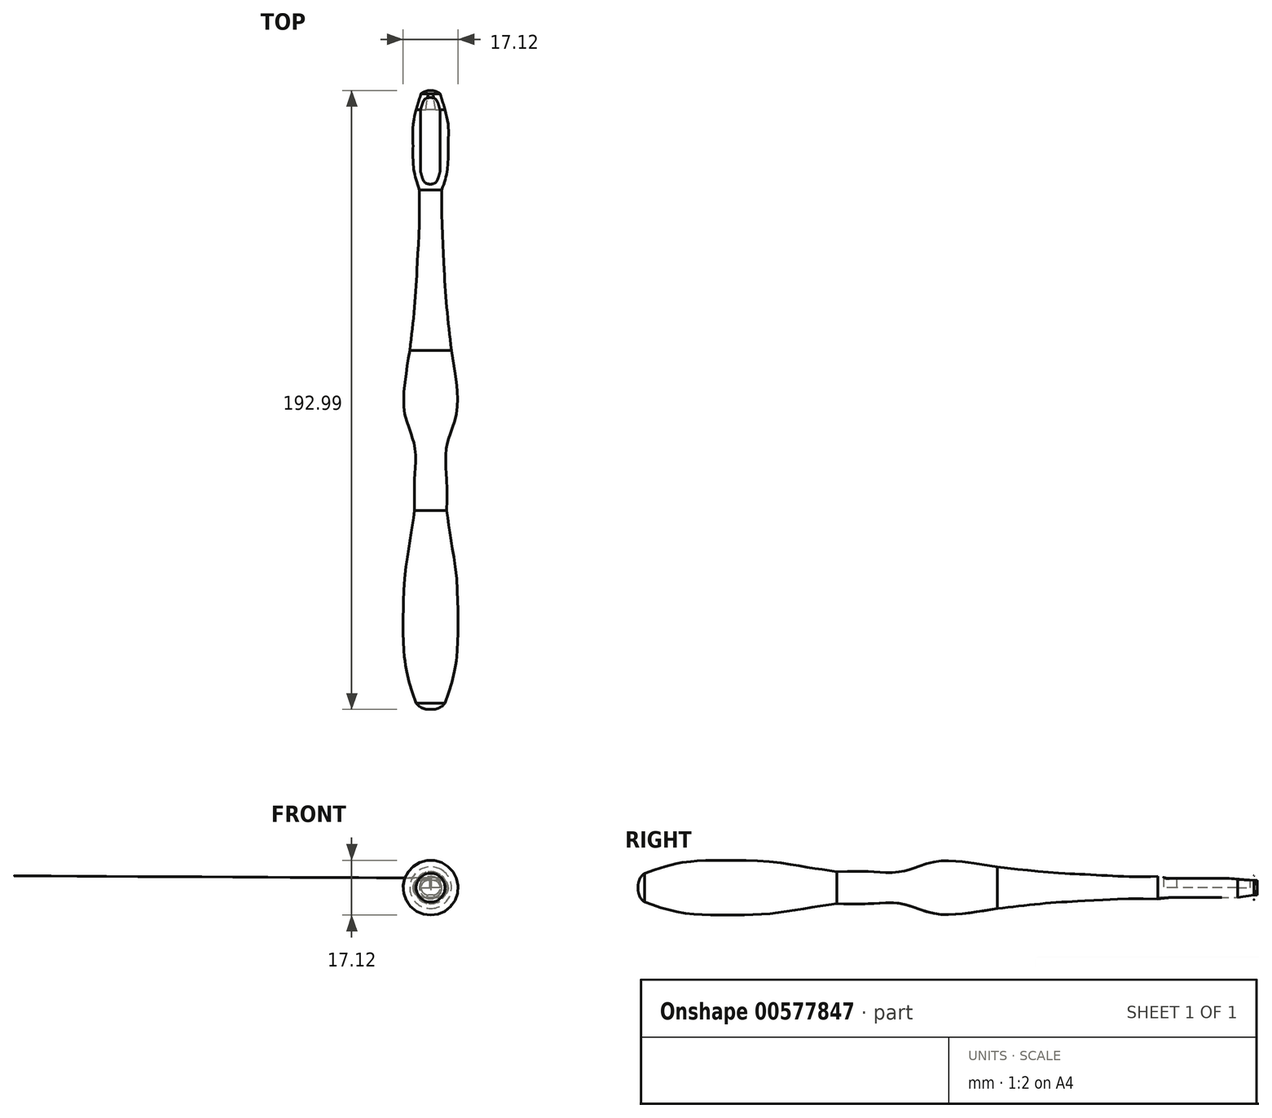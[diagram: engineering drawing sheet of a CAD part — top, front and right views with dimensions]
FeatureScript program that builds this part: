
annotation { "Feature Type Name" : "Feature", "Feature Type Description" : "" }
export const myFeature = defineFeature(function(context is Context, id is Id, definition is map)
    precondition{}
    {
        {
            var Q0;
            Q0=qCreatedBy(makeId("Front.planeOp"),FACE);
            cPlane(context, id + "F0", {"entities" : qUnion([Q0]), "cplaneType" : CPlaneType.OFFSET, "offset" : 10 * mm, "oppositeDirection" : true, "width" : 150 * mm, "height" : 150 * mm});
        }
        {
            var Q0;
            Q0=qCreatedBy(id+"F0.planeOp",FACE);
            cPlane(context, id + "F1", {"entities" : qUnion([Q0]), "cplaneType" : CPlaneType.OFFSET, "offset" : 10 * mm, "oppositeDirection" : true, "width" : 150 * mm, "height" : 150 * mm});
        }
        {
            var Q0;
            Q0=qCreatedBy(id+"F1.planeOp",FACE);
            cPlane(context, id + "F2", {"entities" : qUnion([Q0]), "cplaneType" : CPlaneType.OFFSET, "offset" : 10 * mm, "oppositeDirection" : true, "width" : 150 * mm, "height" : 150 * mm});
        }
        {
            var Q0;
            Q0=qCreatedBy(id+"F2.planeOp",FACE);
            cPlane(context, id + "F3", {"entities" : qUnion([Q0]), "cplaneType" : CPlaneType.OFFSET, "offset" : 10 * mm, "oppositeDirection" : true, "width" : 150 * mm, "height" : 150 * mm});
        }
        {
            var Q0;
            Q0=qCreatedBy(id+"F3.planeOp",FACE);
            cPlane(context, id + "F4", {"entities" : qUnion([Q0]), "cplaneType" : CPlaneType.OFFSET, "offset" : 10 * mm, "oppositeDirection" : true, "width" : 150 * mm, "height" : 150 * mm});
        }
        {
            var Q0;
            Q0=qCreatedBy(id+"F4.planeOp",FACE);
            cPlane(context, id + "F5", {"entities" : qUnion([Q0]), "cplaneType" : CPlaneType.OFFSET, "offset" : 10 * mm, "oppositeDirection" : true, "width" : 150 * mm, "height" : 150 * mm});
        }
        {
            var Q0;
            Q0=qCreatedBy(id+"F5.planeOp",FACE);
            cPlane(context, id + "F6", {"entities" : qUnion([Q0]), "cplaneType" : CPlaneType.OFFSET, "offset" : 10 * mm, "oppositeDirection" : true, "width" : 150 * mm, "height" : 150 * mm});
        }
        {
            var Q0;
            Q0=qCreatedBy(id+"F6.planeOp",FACE);
            cPlane(context, id + "F7", {"entities" : qUnion([Q0]), "cplaneType" : CPlaneType.OFFSET, "offset" : 10 * mm, "oppositeDirection" : true, "width" : 150 * mm, "height" : 150 * mm});
        }
        {
            var Q0;
            Q0=qCreatedBy(id+"F7.planeOp",FACE);
            cPlane(context, id + "F8", {"entities" : qUnion([Q0]), "cplaneType" : CPlaneType.OFFSET, "offset" : 10 * mm, "oppositeDirection" : true, "width" : 150 * mm, "height" : 150 * mm});
        }
        {
            var Q0;
            Q0=qCreatedBy(id+"F8.planeOp",FACE);
            cPlane(context, id + "F9", {"entities" : qUnion([Q0]), "cplaneType" : CPlaneType.OFFSET, "offset" : 10 * mm, "oppositeDirection" : true, "width" : 150 * mm, "height" : 150 * mm});
        }
        {
            var Q0;
            Q0=qCreatedBy(id+"F0.planeOp",FACE);
            var sketch = newSketch(context, id + "F10", { "sketchPlane" : qUnion([Q0])});
            skCircle(sketch, "E0", {"center": v(0, 0) * mm, "radius": 4.5 * mm});
            skSolve(sketch);
        }
        {
            var Q0;
            Q0=qCreatedBy(id+"F1.planeOp",FACE);
            var sketch = newSketch(context, id + "F11", { "sketchPlane" : qUnion([Q0])});
            skCircle(sketch, "E1", {"center": v(0, 0) * mm, "radius": 7.5 * mm});
            skSolve(sketch);
        }
        {
            var Q0;
            Q0=qCreatedBy(id+"F2.planeOp",FACE);
            var sketch = newSketch(context, id + "F12", { "sketchPlane" : qUnion([Q0])});
            skCircle(sketch, "E2", {"center": v(0, 0) * mm, "radius": 8.5 * mm});
            skSolve(sketch);
        }
        {
            var Q0;
            Q0=qCreatedBy(id+"F3.planeOp",FACE);
            var sketch = newSketch(context, id + "F13", { "sketchPlane" : qUnion([Q0])});
            skCircle(sketch, "E3", {"center": v(0, 0) * mm, "radius": 8.5 * mm});
            skSolve(sketch);
        }
        {
            var Q0;
            Q0=qCreatedBy(id+"F4.planeOp",FACE);
            var sketch = newSketch(context, id + "F14", { "sketchPlane" : qUnion([Q0])});
            skCircle(sketch, "E4", {"center": v(0, 0) * mm, "radius": 8 * mm});
            skSolve(sketch);
        }
        {
            var Q0;
            Q0=qCreatedBy(id+"F5.planeOp",FACE);
            var sketch = newSketch(context, id + "F15", { "sketchPlane" : qUnion([Q0])});
            skCircle(sketch, "E5", {"center": v(0, 0) * mm, "radius": 6.5 * mm});
            skSolve(sketch);
        }
        {
            var Q0;
            Q0=qCreatedBy(id+"F6.planeOp",FACE);
            var sketch = newSketch(context, id + "F16", { "sketchPlane" : qUnion([Q0])});
            skCircle(sketch, "E6", {"center": v(0, 0) * mm, "radius": 5 * mm});
            skSolve(sketch);
        }
        {
            var Q0;
            Q0=qCreatedBy(id+"F7.planeOp",FACE);
            var sketch = newSketch(context, id + "F17", { "sketchPlane" : qUnion([Q0])});
            skCircle(sketch, "E7", {"center": v(0, 0) * mm, "radius": 5 * mm});
            skSolve(sketch);
        }
        {
            var Q0;
            Q0=qCreatedBy(id+"F8.planeOp",FACE);
            var sketch = newSketch(context, id + "F18", { "sketchPlane" : qUnion([Q0])});
            skCircle(sketch, "E8", {"center": v(0, 0) * mm, "radius": 5 * mm});
            skSolve(sketch);
        }
        {
            var Q0;
            Q0=qCreatedBy(id+"F9.planeOp",FACE);
            var sketch = newSketch(context, id + "F19", { "sketchPlane" : qUnion([Q0])});
            skCircle(sketch, "E9", {"center": v(0, 0) * mm, "radius": 8 * mm});
            skSolve(sketch);
        }
        {
            var Q0;
            Q0=qCreatedBy(id+"F9.planeOp",FACE);
            cPlane(context, id + "F20", {"entities" : qUnion([Q0]), "cplaneType" : CPlaneType.OFFSET, "offset" : 10 * mm, "oppositeDirection" : true, "width" : 150 * mm, "height" : 150 * mm});
        }
        {
            var Q0;
            Q0=qCreatedBy(id+"F20.planeOp",FACE);
            cPlane(context, id + "F21", {"entities" : qUnion([Q0]), "cplaneType" : CPlaneType.OFFSET, "offset" : 10 * mm, "oppositeDirection" : true, "width" : 150 * mm, "height" : 150 * mm});
        }
        {
            var Q0;
            Q0=qCreatedBy(id+"F21.planeOp",FACE);
            cPlane(context, id + "F22", {"entities" : qUnion([Q0]), "cplaneType" : CPlaneType.OFFSET, "offset" : 10 * mm, "oppositeDirection" : true, "width" : 150 * mm, "height" : 150 * mm});
        }
        {
            var Q0;
            Q0=qCreatedBy(id+"F22.planeOp",FACE);
            cPlane(context, id + "F23", {"entities" : qUnion([Q0]), "cplaneType" : CPlaneType.OFFSET, "offset" : 10 * mm, "oppositeDirection" : true, "width" : 150 * mm, "height" : 150 * mm});
        }
        {
            var Q0;
            Q0=qCreatedBy(id+"F23.planeOp",FACE);
            cPlane(context, id + "F24", {"entities" : qUnion([Q0]), "cplaneType" : CPlaneType.OFFSET, "offset" : 10 * mm, "oppositeDirection" : true, "width" : 150 * mm, "height" : 150 * mm});
        }
        {
            var Q0;
            Q0=qCreatedBy(id+"F24.planeOp",FACE);
            cPlane(context, id + "F25", {"entities" : qUnion([Q0]), "cplaneType" : CPlaneType.OFFSET, "offset" : 10 * mm, "oppositeDirection" : true, "width" : 150 * mm, "height" : 150 * mm});
        }
        {
            var Q0;
            Q0=qCreatedBy(id+"F20.planeOp",FACE);
            var sketch = newSketch(context, id + "F26", { "sketchPlane" : qUnion([Q0])});
            skCircle(sketch, "E10", {"center": v(0, 0) * mm, "radius": 8 * mm});
            skSolve(sketch);
        }
        {
            var Q0;
            Q0=qCreatedBy(id+"F21.planeOp",FACE);
            var sketch = newSketch(context, id + "F27", { "sketchPlane" : qUnion([Q0])});
            skCircle(sketch, "E11", {"center": v(0, 0) * mm, "radius": 6.5 * mm});
            skSolve(sketch);
        }
        {
            var Q0;
            Q0=qCreatedBy(id+"F23.planeOp",FACE);
            var sketch = newSketch(context, id + "F28", { "sketchPlane" : qUnion([Q0])});
            skCircle(sketch, "E12", {"center": v(0, 0) * mm, "radius": 4.5 * mm});
            skSolve(sketch);
        }
        {
            var Q0;
            Q0=qCreatedBy(id+"F24.planeOp",FACE);
            var sketch = newSketch(context, id + "F29", { "sketchPlane" : qUnion([Q0])});
            skCircle(sketch, "E13", {"center": v(0, 0) * mm, "radius": 4 * mm});
            skSolve(sketch);
        }
        {
            var Q0;
            Q0=qCreatedBy(id+"F25.planeOp",FACE);
            var sketch = newSketch(context, id + "F30", { "sketchPlane" : qUnion([Q0])});
            skCircle(sketch, "E14", {"center": v(0, 0) * mm, "radius": 3.5 * mm});
            skSolve(sketch);
        }
        {
            var Q0;
            Q0=qCreatedBy(id+"F25.planeOp",FACE);
            cPlane(context, id + "F31", {"entities" : qUnion([Q0]), "cplaneType" : CPlaneType.OFFSET, "offset" : 10 * mm, "oppositeDirection" : true, "width" : 150 * mm, "height" : 150 * mm});
        }
        {
            var Q0;
            Q0=qCreatedBy(id+"F31.planeOp",FACE);
            var sketch = newSketch(context, id + "F32", { "sketchPlane" : qUnion([Q0])});
            skCircle(sketch, "E15", {"center": v(0, 0) * mm, "radius": 3.5 * mm});
            skSolve(sketch);
        }
        {
            var Q0;
            Q0=makeQuery(id+"F10.imprint","IMPRINT",FACE,{"disambiguationData":[TD([[makeQuery(id+"F10.imprint","IMPRINT",EDGE,{"derivedFrom":sQuery(id+"F10.wireOp",EDGE,"E0")}),1.0]])]});
            var Q1;
            Q1=makeQuery(id+"F11.imprint","IMPRINT",FACE,{"disambiguationData":[TD([[makeQuery(id+"F11.imprint","IMPRINT",EDGE,{"derivedFrom":sQuery(id+"F11.wireOp",EDGE,"E1")}),1.0]])]});
            var Q2;
            Q2=makeQuery(id+"F12.imprint","IMPRINT",FACE,{"disambiguationData":[TD([[makeQuery(id+"F12.imprint","IMPRINT",EDGE,{"derivedFrom":sQuery(id+"F12.wireOp",EDGE,"E2")}),1.0]])]});
            var Q3;
            Q3=makeQuery(id+"F13.imprint","IMPRINT",FACE,{"disambiguationData":[TD([[makeQuery(id+"F13.imprint","IMPRINT",EDGE,{"derivedFrom":sQuery(id+"F13.wireOp",EDGE,"E3")}),1.0]])]});
            var Q4;
            Q4=makeQuery(id+"F14.imprint","IMPRINT",FACE,{"disambiguationData":[TD([[makeQuery(id+"F14.imprint","IMPRINT",EDGE,{"derivedFrom":sQuery(id+"F14.wireOp",EDGE,"E4")}),1.0]])]});
            var Q5;
            Q5=makeQuery(id+"F15.imprint","IMPRINT",FACE,{"disambiguationData":[TD([[makeQuery(id+"F15.imprint","IMPRINT",EDGE,{"derivedFrom":sQuery(id+"F15.wireOp",EDGE,"E5")}),1.0]])]});
            var Q6;
            Q6=makeQuery(id+"F16.imprint","IMPRINT",FACE,{"disambiguationData":[TD([[makeQuery(id+"F16.imprint","IMPRINT",EDGE,{"derivedFrom":sQuery(id+"F16.wireOp",EDGE,"E6")}),1.0]])]});
            loft(context, id + "F33", {"sheetProfilesArray" : [{ "sheetProfileEntities" : qUnion([Q0]) }, { "sheetProfileEntities" : qUnion([Q1]) }, { "sheetProfileEntities" : qUnion([Q2]) }, { "sheetProfileEntities" : qUnion([Q3]) }, { "sheetProfileEntities" : qUnion([Q4]) }, { "sheetProfileEntities" : qUnion([Q5]) }, { "sheetProfileEntities" : qUnion([Q6]) }]});
        }
        {
            var Q1;
            Q1=makeQuery(id+"F33.opLoft","CAP_FACE",FACE,{"disambiguationData":[OSD([makeQuery(id+"F16.imprint","IMPRINT",FACE,{"disambiguationData":[TD([[makeQuery(id+"F16.imprint","IMPRINT",EDGE,{"derivedFrom":sQuery(id+"F16.wireOp",EDGE,"E6")}),1.0]])]})])],"isStart":true});
            var Q2;
            Q2=makeQuery(id+"F17.imprint","IMPRINT",FACE,{"disambiguationData":[TD([[makeQuery(id+"F17.imprint","IMPRINT",EDGE,{"derivedFrom":sQuery(id+"F17.wireOp",EDGE,"E7")}),1.0]])]});
            var Q3;
            Q3=makeQuery(id+"F18.imprint","IMPRINT",FACE,{"disambiguationData":[TD([[makeQuery(id+"F18.imprint","IMPRINT",EDGE,{"derivedFrom":sQuery(id+"F18.wireOp",EDGE,"E8")}),1.0]])]});
            var Q4;
            Q4=makeQuery(id+"F19.imprint","IMPRINT",FACE,{"disambiguationData":[TD([[makeQuery(id+"F19.imprint","IMPRINT",EDGE,{"derivedFrom":sQuery(id+"F19.wireOp",EDGE,"E9")}),1.0]])]});
            var Q5;
            Q5=makeQuery(id+"F26.imprint","IMPRINT",FACE,{"disambiguationData":[TD([[makeQuery(id+"F26.imprint","IMPRINT",EDGE,{"derivedFrom":sQuery(id+"F26.wireOp",EDGE,"E10")}),1.0]])]});
            var Q6;
            Q6=makeQuery(id+"F27.imprint","IMPRINT",FACE,{"disambiguationData":[TD([[makeQuery(id+"F27.imprint","IMPRINT",EDGE,{"derivedFrom":sQuery(id+"F27.wireOp",EDGE,"E11")}),1.0]])]});
            loft(context, id + "F34", {"operationType" : NewBodyOperationType.ADD, "sheetProfilesArray" : [{ "sheetProfileEntities" : qUnion([Q1]) }, { "sheetProfileEntities" : qUnion([Q2]) }, { "sheetProfileEntities" : qUnion([Q3]) }, { "sheetProfileEntities" : qUnion([Q4]) }, { "sheetProfileEntities" : qUnion([Q5]) }, { "sheetProfileEntities" : qUnion([Q6]) }]});
        }
        {
            var Q1;
            Q1=makeQuery(id+"F34.opLoft","CAP_FACE",FACE,{"disambiguationData":[OSD([makeQuery(id+"F27.imprint","IMPRINT",FACE,{"disambiguationData":[TD([[makeQuery(id+"F27.imprint","IMPRINT",EDGE,{"derivedFrom":sQuery(id+"F27.wireOp",EDGE,"E11")}),1.0]])]})])],"isStart":true});
            var Q2;
            Q2 = qSketchRegion(id + "F28", true);
            var Q3;
            Q3 = qSketchRegion(id + "F29", true);
            var Q4;
            Q4 = qSketchRegion(id + "F30", true);
            var Q5;
            Q5 = qSketchRegion(id + "F32", true);
            loft(context, id + "F35", {"operationType" : NewBodyOperationType.ADD, "sheetProfilesArray" : [{ "sheetProfileEntities" : qUnion([Q1]) }, { "sheetProfileEntities" : qUnion([Q2]) }, { "sheetProfileEntities" : qUnion([Q3]) }, { "sheetProfileEntities" : qUnion([Q4]) }, { "sheetProfileEntities" : qUnion([Q5]) }]});
        }
        {
            var Q0;
            Q0=qCreatedBy(id+"F0.planeOp",FACE);
            cPlane(context, id + "F36", {"entities" : qUnion([Q0]), "cplaneType" : CPlaneType.OFFSET, "offset" : 2 * mm, "width" : 150 * mm, "height" : 150 * mm});
        }
        {
            var Q0;
            Q0=qCreatedBy(id+"F36.planeOp",FACE);
            var sketch = newSketch(context, id + "F37", { "sketchPlane" : qUnion([Q0])});
            skCircle(sketch, "E16", {"center": v(0, 0) * mm, "radius": 3 * mm});
            skSolve(sketch);
        }
        {
            var Q1;
            Q1=makeQuery(id+"F33.opLoft","CAP_FACE",FACE,{"disambiguationData":[OSD([makeQuery(id+"F10.imprint","IMPRINT",FACE,{"disambiguationData":[TD([[makeQuery(id+"F10.imprint","IMPRINT",EDGE,{"derivedFrom":sQuery(id+"F10.wireOp",EDGE,"E0")}),1.0]])]})])],"isStart":true});
            var Q2;
            Q2 = qSketchRegion(id + "F37", true);
            loft(context, id + "F38", {"operationType" : NewBodyOperationType.ADD, "sheetProfilesArray" : [{ "sheetProfileEntities" : qUnion([Q1]) }, { "sheetProfileEntities" : qUnion([Q2]) }]});
        }
        {
            var Q0;
            Q0=makeQuery(id+"F38.opLoft","MID_CAP_EDGE",EDGE,{"disambiguationData":[OSD([sQuery(id+"F10.wireOp",EDGE,"E0"),sQuery(id+"F37.wireOp",EDGE,"E16")])],"capPos":1.0});
            fillet(context, id + "F39", {"entities" : qUnion([Q0]), "radius" : 5 * mm, "tangentPropagation" : true, "allowEdgeOverflow" : false});
        }
        {
            var Q0;
            Q0=qCreatedBy(id+"F31.planeOp",FACE);
            cPlane(context, id + "F40", {"entities" : qUnion([Q0]), "cplaneType" : CPlaneType.OFFSET, "offset" : 5 * mm, "oppositeDirection" : true, "width" : 150 * mm, "height" : 150 * mm});
        }
        {
            var Q0;
            Q0=qCreatedBy(id+"F40.planeOp",FACE);
            cPlane(context, id + "F41", {"entities" : qUnion([Q0]), "cplaneType" : CPlaneType.OFFSET, "offset" : 5 * mm, "oppositeDirection" : true, "width" : 150 * mm, "height" : 150 * mm});
        }
        {
            var Q0;
            Q0=qCreatedBy(id+"F41.planeOp",FACE);
            cPlane(context, id + "F42", {"entities" : qUnion([Q0]), "cplaneType" : CPlaneType.OFFSET, "offset" : 5 * mm, "oppositeDirection" : true, "width" : 150 * mm, "height" : 150 * mm});
        }
        {
            var Q0;
            Q0=qCreatedBy(id+"F42.planeOp",FACE);
            cPlane(context, id + "F43", {"entities" : qUnion([Q0]), "cplaneType" : CPlaneType.OFFSET, "offset" : 5 * mm, "oppositeDirection" : true, "width" : 150 * mm, "height" : 150 * mm});
        }
        {
            var Q0;
            Q0=qCreatedBy(id+"F43.planeOp",FACE);
            cPlane(context, id + "F44", {"entities" : qUnion([Q0]), "cplaneType" : CPlaneType.OFFSET, "offset" : 5 * mm, "oppositeDirection" : true, "width" : 150 * mm, "height" : 150 * mm});
        }
        {
            var Q0;
            Q0=qCreatedBy(id+"F40.planeOp",FACE);
            var sketch = newSketch(context, id + "F45", { "sketchPlane" : qUnion([Q0])});
            skLineSegment(sketch, "E17.bottom", {"start": v(2, 3) * mm, "end": v(-2, 3) * mm});
            skLineSegment(sketch, "E17.top", {"start": v(2, -3) * mm, "end": v(-2, -3) * mm});
            skPoint(sketch, "E17.middle", {"position": v(0, 0) * mm});
            skArc(sketch, "E18", {"start": v(2, -3) * mm, "mid": v(5, 0) * mm, "end": v(2, 3) * mm});
            skArc(sketch, "E19", {"start": v(-2, 3) * mm, "mid": v(-5, 0) * mm, "end": v(-2, -3) * mm});
            skSolve(sketch);
        }
        {
            var Q0;
            Q0=qCreatedBy(id+"F41.planeOp",FACE);
            var sketch = newSketch(context, id + "F46", { "sketchPlane" : qUnion([Q0])});
            skLineSegment(sketch, "E20.bottom", {"start": v(2.5, 3) * mm, "end": v(-2.5, 3) * mm});
            skLineSegment(sketch, "E20.top", {"start": v(2.5, -3) * mm, "end": v(-2.5, -3) * mm});
            skPoint(sketch, "E20.middle", {"position": v(0, 0) * mm});
            skArc(sketch, "E21", {"start": v(2.5, -3) * mm, "mid": v(5.5, 0) * mm, "end": v(2.5, 3) * mm});
            skArc(sketch, "E22", {"start": v(-2.5, 3) * mm, "mid": v(-5.5, 0) * mm, "end": v(-2.5, -3) * mm});
            skSolve(sketch);
        }
        {
            var Q0;
            Q0=qCreatedBy(id+"F42.planeOp",FACE);
            var sketch = newSketch(context, id + "F47", { "sketchPlane" : qUnion([Q0])});
            skLineSegment(sketch, "E23.0.0", {"start": v(-2.5, -3) * mm, "end": v(2.5, -3) * mm});
            skArc(sketch, "E23.0.1", {"start": v(2.5, -3) * mm, "mid": v(5.5, 0) * mm, "end": v(2.5, 3) * mm});
            skLineSegment(sketch, "E23.0.2", {"start": v(2.5, 3) * mm, "end": v(-2.5, 3) * mm});
            skArc(sketch, "E23.0.3", {"start": v(-2.5, 3) * mm, "mid": v(-5.5, 0) * mm, "end": v(-2.5, -3) * mm});
            skSolve(sketch);
        }
        {
            var Q0;
            Q0=qCreatedBy(id+"F43.planeOp",FACE);
            var sketch = newSketch(context, id + "F48", { "sketchPlane" : qUnion([Q0])});
            skLineSegment(sketch, "E24.0.0", {"start": v(2.5, 3) * mm, "end": v(-2.5, 3) * mm});
            skArc(sketch, "E24.0.1", {"start": v(-2.5, 3) * mm, "mid": v(-5.5, 0) * mm, "end": v(-2.5, -3) * mm});
            skLineSegment(sketch, "E24.0.2", {"start": v(-2.5, -3) * mm, "end": v(2.5, -3) * mm});
            skArc(sketch, "E24.0.3", {"start": v(2.5, -3) * mm, "mid": v(5.5, 0) * mm, "end": v(2.5, 3) * mm});
            skSolve(sketch);
        }
        {
            var Q0;
            Q0=qCreatedBy(id+"F44.planeOp",FACE);
            var sketch = newSketch(context, id + "F49", { "sketchPlane" : qUnion([Q0])});
            skLineSegment(sketch, "E25.bottom", {"start": v(1.5, 3) * mm, "end": v(-1.5, 3) * mm});
            skLineSegment(sketch, "E25.top", {"start": v(1.5, -3) * mm, "end": v(-1.5, -3) * mm});
            skPoint(sketch, "E25.middle", {"position": v(0, 0) * mm});
            skArc(sketch, "E26", {"start": v(1.5, -3) * mm, "mid": v(4.5, 0) * mm, "end": v(1.5, 3) * mm});
            skArc(sketch, "E27", {"start": v(-1.5, 3) * mm, "mid": v(-4.5, 0) * mm, "end": v(-1.5, -3) * mm});
            skSolve(sketch);
        }
        {
            var Q0;
            Q0=qCreatedBy(id+"F44.planeOp",FACE);
            cPlane(context, id + "F50", {"entities" : qUnion([Q0]), "cplaneType" : CPlaneType.OFFSET, "offset" : 5 * mm, "oppositeDirection" : true, "width" : 150 * mm, "height" : 150 * mm});
        }
        {
            var Q0;
            Q0=qCreatedBy(id+"F50.planeOp",FACE);
            var sketch = newSketch(context, id + "F51", { "sketchPlane" : qUnion([Q0])});
            skLineSegment(sketch, "E28.bottom", {"start": v(0.75, 2.25) * mm, "end": v(-0.75, 2.25) * mm});
            skLineSegment(sketch, "E28.top", {"start": v(0.75, -2.25) * mm, "end": v(-0.75, -2.25) * mm});
            skPoint(sketch, "E28.middle", {"position": v(0, 0) * mm});
            skArc(sketch, "E29", {"start": v(0.75, -2.25) * mm, "mid": v(3, 0) * mm, "end": v(0.75, 2.25) * mm});
            skArc(sketch, "E30", {"start": v(-0.75, 2.25) * mm, "mid": v(-3, 0) * mm, "end": v(-0.75, -2.25) * mm});
            skSolve(sketch);
        }
        {
            var Q1;
            Q1=makeQuery(id+"F35.opLoft","CAP_FACE",FACE,{"disambiguationData":[OSD([makeQuery(id+"F32.imprint","IMPRINT",FACE,{"disambiguationData":[TD([[makeQuery(id+"F32.imprint","IMPRINT",EDGE,{"derivedFrom":sQuery(id+"F32.wireOp",EDGE,"E15")}),1.0]])]})])],"isStart":true});
            var Q2;
            Q2=makeQuery(id+"F45.imprint","IMPRINT",FACE,{"disambiguationData":[TD([[makeQuery(id+"F45.imprint","IMPRINT",EDGE,{"derivedFrom":sQuery(id+"F45.wireOp",EDGE,"E17.bottom")}),1.0]])]});
            var Q3;
            Q3=makeQuery(id+"F46.imprint","IMPRINT",FACE,{"disambiguationData":[TD([[makeQuery(id+"F46.imprint","IMPRINT",EDGE,{"derivedFrom":sQuery(id+"F46.wireOp",EDGE,"E20.bottom")}),1.0]])]});
            var Q4;
            Q4=makeQuery(id+"F47.imprint","IMPRINT",FACE,{"disambiguationData":[TD([[makeQuery(id+"F47.imprint","IMPRINT",EDGE,{"derivedFrom":sQuery(id+"F47.wireOp",EDGE,"E23.0.0")}),1.0]])]});
            var Q5;
            Q5=makeQuery(id+"F48.imprint","IMPRINT",FACE,{"disambiguationData":[TD([[makeQuery(id+"F48.imprint","IMPRINT",EDGE,{"derivedFrom":sQuery(id+"F48.wireOp",EDGE,"E24.0.0")}),1.0]])]});
            var Q6;
            Q6=makeQuery(id+"F49.imprint","IMPRINT",FACE,{"disambiguationData":[TD([[makeQuery(id+"F49.imprint","IMPRINT",EDGE,{"derivedFrom":sQuery(id+"F49.wireOp",EDGE,"E25.bottom")}),1.0]])]});
            loft(context, id + "F52", {"operationType" : NewBodyOperationType.ADD, "sheetProfilesArray" : [{ "sheetProfileEntities" : qUnion([Q1]) }, { "sheetProfileEntities" : qUnion([Q2]) }, { "sheetProfileEntities" : qUnion([Q3]) }, { "sheetProfileEntities" : qUnion([Q4]) }, { "sheetProfileEntities" : qUnion([Q5]) }, { "sheetProfileEntities" : qUnion([Q6]) }]});
        }
        {
            var Q1;
            Q1=makeQuery(id+"F52.opLoft","CAP_FACE",FACE,{"disambiguationData":[OSD([makeQuery(id+"F49.imprint","IMPRINT",FACE,{"disambiguationData":[TD([[makeQuery(id+"F49.imprint","IMPRINT",EDGE,{"derivedFrom":sQuery(id+"F49.wireOp",EDGE,"E25.bottom")}),1.0]])]})])],"isStart":true});
            var Q2;
            Q2=makeQuery(id+"F51.imprint","IMPRINT",FACE,{"disambiguationData":[TD([[makeQuery(id+"F51.imprint","IMPRINT",EDGE,{"derivedFrom":sQuery(id+"F51.wireOp",EDGE,"E28.bottom")}),1.0]])]});
            loft(context, id + "F53", {"operationType" : NewBodyOperationType.ADD, "sheetProfilesArray" : [{ "sheetProfileEntities" : qUnion([Q1]) }, { "sheetProfileEntities" : qUnion([Q2]) }]});
        }
        {
            var Q0;
            Q0=qCreatedBy(id+"F50.planeOp",FACE);
            cPlane(context, id + "F54", {"entities" : qUnion([Q0]), "cplaneType" : CPlaneType.OFFSET, "offset" : 1 * mm, "oppositeDirection" : true, "width" : 150 * mm, "height" : 150 * mm});
        }
        {
            var Q0;
            Q0=qCreatedBy(makeId("Top.planeOp"),FACE);
            var sketch = newSketch(context, id + "F55", { "sketchPlane" : qUnion([Q0])});
            skFitSpline(sketch, "E31", {"points": [v(-3.2, 194.73) * mm, v(-2.59, 196.8) * mm, v(-1.7, 198.37) * mm, v(-0.4, 198.79) * mm], "startDerivative": vector(1.51, 5.63) * mm, "endDerivative": vector(4.83, 0.66) * mm});
            skLineSegment(sketch, "E32.bottom", {"start": v(-3.2, 194.73) * mm, "end": v(3, 194.73) * mm});
            skLineSegment(sketch, "E32.top", {"start": v(-3.2, 175.86) * mm, "end": v(3, 175.86) * mm});
            skLineSegment(sketch, "E32.left", {"start": v(-3.2, 194.73) * mm, "end": v(-3.2, 175.86) * mm});
            skLineSegment(sketch, "E32.right", {"start": v(3, 194.73) * mm, "end": v(3, 175.86) * mm});
            skLineSegment(sketch, "E33", {"start": v(-3.2, 185.3) * mm, "end": v(8.03, 185.3) * mm, "construction": true});
            skPoint(sketch, "E33.endSnap0", {"position": v(3, 185.3) * mm});
            skLineSegment(sketch, "E34", {"start": v(-0.1, 194.73) * mm, "end": v(-0.1, 186.67) * mm, "construction": true});
            skFitSpline(sketch, "E35.MirrorCS", {"points": [v(3, 194.73) * mm, v(2.38, 196.8) * mm, v(1.5, 198.37) * mm, v(0.19, 198.79) * mm], "startDerivative": vector(-1.51, 5.63) * mm, "endDerivative": vector(-4.83, 0.66) * mm});
            skLineSegment(sketch, "E36.MirrorCS", {"start": v(3, 185.3) * mm, "end": v(-8.23, 185.3) * mm, "construction": true});
            skFitSpline(sketch, "E37.MirrorCS", {"points": [v(-3.2, 175.86) * mm, v(-2.59, 173.8) * mm, v(-1.7, 172.22) * mm, v(-0.4, 171.8) * mm], "startDerivative": vector(1.51, -5.63) * mm, "endDerivative": vector(4.83, -0.66) * mm});
            skFitSpline(sketch, "E38.MirrorCS", {"points": [v(3, 175.86) * mm, v(2.38, 173.8) * mm, v(1.5, 172.22) * mm, v(0.19, 171.8) * mm], "startDerivative": vector(-1.51, -5.63) * mm, "endDerivative": vector(-4.83, -0.66) * mm});
            skFitSpline(sketch, "E39", {"points": [v(-0.4, 198.79) * mm, v(0.19, 198.79) * mm], "startDerivative": vector(0.58, 0) * mm, "endDerivative": vector(0.58, 0) * mm});
            skFitSpline(sketch, "E40", {"points": [v(-0.4, 171.8) * mm, v(0.19, 171.8) * mm], "startDerivative": vector(0.58, 0) * mm, "endDerivative": vector(0.58, 0) * mm});
            skSolve(sketch);
        }
        {
            var Q0;
            Q0 = qSketchRegion(id + "F55", true);
            extrude(context, id + "F56", {"entities" : qUnion([Q0]), "operationType" : NewBodyOperationType.REMOVE, "depth" : 5 * mm, "offsetDistance" : 25 * mm});
        }
        {
            var Q0;
            Q0=qCreatedBy(makeId("Top.planeOp"),FACE);
            var sketch = newSketch(context, id + "F57", { "sketchPlane" : qUnion([Q0])});
            skLineSegment(sketch, "E41", {"start": v(0, 200) * mm, "end": v(0, 202.47) * mm, "construction": true});
            skLineSegment(sketch, "E42", {"start": v(0, 200) * mm, "end": v(-3, 200) * mm});
            skArc(sketch, "E43", {"start": v(0, 201) * mm, "mid": v(-1.58, 200.75) * mm, "end": v(-3, 200) * mm});
            skArc(sketch, "E44.MirrorCS", {"start": v(0, 201) * mm, "mid": v(1.58, 200.75) * mm, "end": v(3, 200) * mm});
            skLineSegment(sketch, "E45.MirrorCS", {"start": v(0, 200) * mm, "end": v(3, 200) * mm});
            skSolve(sketch);
        }
        {
            var Q0;
            Q0=makeQuery(id+"F57.imprint","IMPRINT",FACE,{"disambiguationData":[TD([[makeQuery(id+"F57.imprint","IMPRINT",EDGE,{"derivedFrom":sQuery(id+"F57.wireOp",EDGE,"E42")}),-1.0]])]});
            extrude(context, id + "F58", {"entities" : qUnion([Q0]), "endBound" : BoundingType.SYMMETRIC, "depth" : 7.42 * mm, "offsetDistance" : 25 * mm});
        }
        {
            var Q0;
            Q0=qCreatedBy(id+"F50.planeOp",FACE);
            var sketch = newSketch(context, id + "F59", { "sketchPlane" : qUnion([Q0])});
            skLineSegment(sketch, "E46.0", {"start": v(0.75, 2.25) * mm, "end": v(-0.75, 2.25) * mm});
            skLineSegment(sketch, "E46.1", {"start": v(0.75, -2.25) * mm, "end": v(-0.75, -2.25) * mm});
            skPoint(sketch, "E46.2", {"position": v(0, 0) * mm});
            skArc(sketch, "E46.3", {"start": v(0.75, -2.25) * mm, "mid": v(3, 0) * mm, "end": v(0.75, 2.25) * mm});
            skArc(sketch, "E46.4", {"start": v(-0.75, 2.25) * mm, "mid": v(-3, 0) * mm, "end": v(-0.75, -2.25) * mm});
            skArc(sketch, "E47.0", {"start": v(-0.75, 4.3) * mm, "mid": v(-5.06, 0) * mm, "end": v(-0.75, -4.3) * mm});
            skLineSegment(sketch, "E47.1", {"start": v(0.75, 4.3) * mm, "end": v(-0.75, 4.3) * mm});
            skArc(sketch, "E47.2", {"start": v(0.75, -4.3) * mm, "mid": v(5.06, 0) * mm, "end": v(0.75, 4.3) * mm});
            skLineSegment(sketch, "E47.3", {"start": v(0.75, -4.3) * mm, "end": v(-0.75, -4.3) * mm});
            skSolve(sketch);
        }
        {
            var Q0;
            Q0=makeQuery(id+"F59.imprint","IMPRINT",FACE,{"disambiguationData":[TD([[makeQuery(id+"F59.imprint","IMPRINT",EDGE,{"derivedFrom":sQuery(id+"F59.wireOp",EDGE,"E46.0")}),-1.0]])]});
            extrude(context, id + "F60", {"entities" : qUnion([Q0]), "operationType" : NewBodyOperationType.REMOVE, "oppositeDirection" : true, "depth" : 13.7 * mm, "offsetDistance" : 25 * mm});
        }
    });
